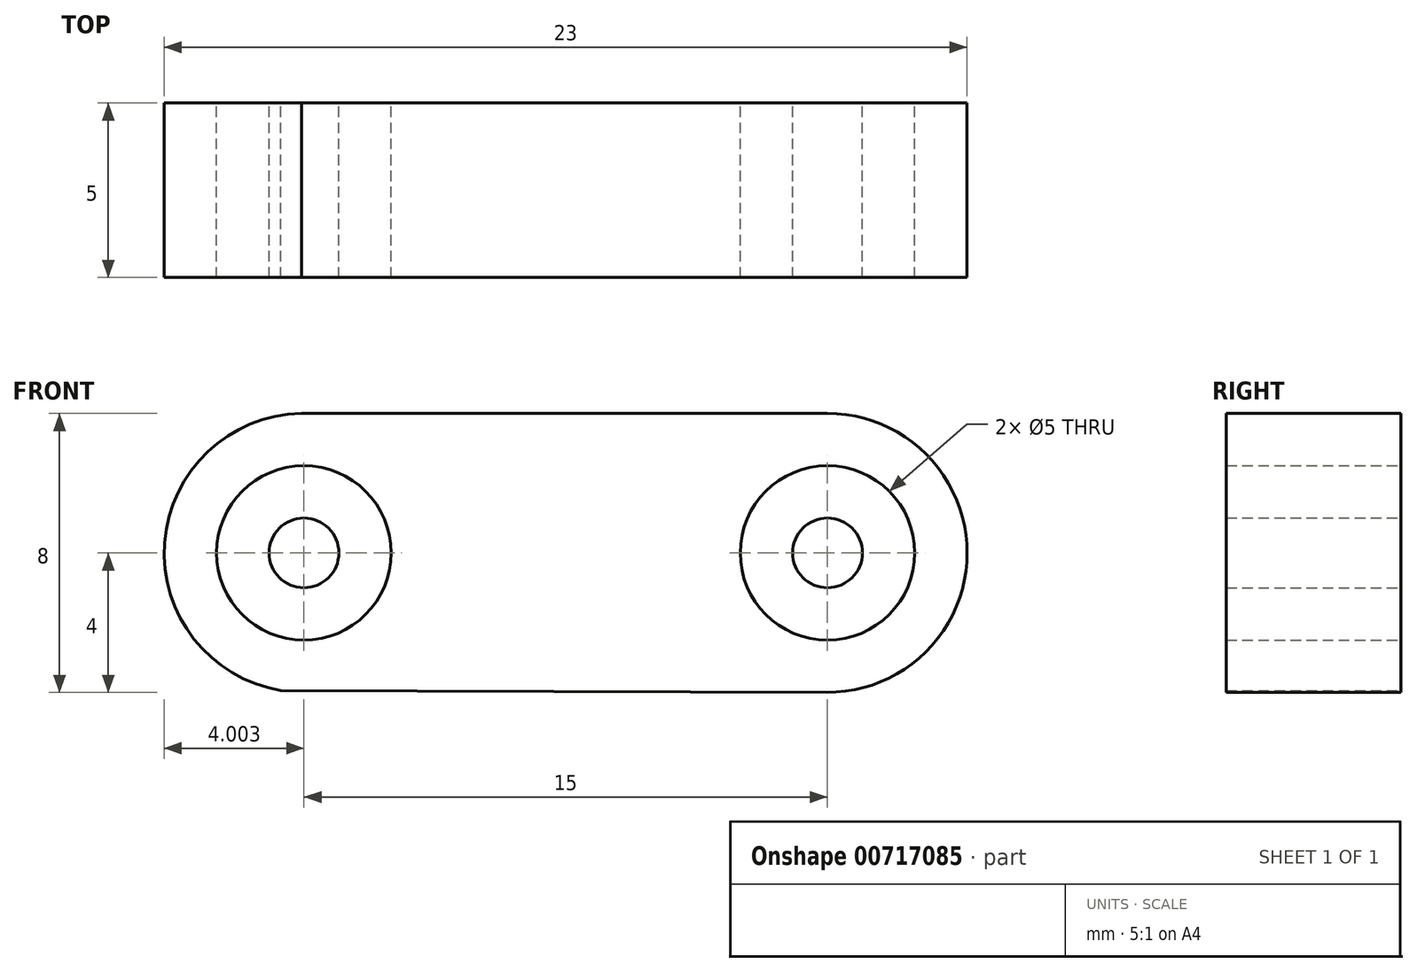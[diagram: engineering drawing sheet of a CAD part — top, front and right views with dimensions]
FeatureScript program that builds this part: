
annotation { "Feature Type Name" : "Feature", "Feature Type Description" : "" }
export const myFeature = defineFeature(function(context is Context, id is Id, definition is map)
    precondition{}
    {
        {
            var Q0;
            Q0=qCreatedBy(makeId("Front.planeOp"),FACE);
            var sketch = newSketch(context, id + "F0", { "sketchPlane" : qUnion([Q0])});
            skLineSegment(sketch, "E0", {"start": v(-11.39, 16.4) * mm, "end": v(3.61, 16.4) * mm});
            skCircle(sketch, "E1", {"center": v(-11.39, 16.4) * mm, "radius": 2.5 * mm});
            skArc(sketch, "E2", {"start": v(-11.31, 20.4) * mm, "mid": v(-15.38, 16.12) * mm, "end": v(-10.75, 12.45) * mm});
            skCircle(sketch, "E3", {"center": v(3.61, 16.4) * mm, "radius": 2.5 * mm});
            skArc(sketch, "E4", {"start": v(3.6, 12.4) * mm, "mid": v(7.61, 16.4) * mm, "end": v(3.61, 20.4) * mm});
            skLineSegment(sketch, "E5", {"start": v(-11.46, 20.4) * mm, "end": v(3.61, 20.4) * mm});
            skLineSegment(sketch, "E6", {"start": v(-12.05, 12.46) * mm, "end": v(3.6, 12.4) * mm});
            skCircle(sketch, "E7", {"center": v(-11.39, 16.4) * mm, "radius": 1 * mm});
            skCircle(sketch, "E8", {"center": v(3.61, 16.4) * mm, "radius": 1 * mm});
            skSolve(sketch);
        }
        {
            var Q0;
            Q0=makeQuery(id+"F0.imprint","IMPRINT",FACE,{"disambiguationData":[TD([[makeQuery(id+"F0.imprint","IMPRINT",EDGE,{"derivedFrom":sQuery(id+"F0.wireOp",EDGE,"E1")}),-1.0]])]});
            extrude(context, id + "F1", {"entities" : qUnion([Q0]), "depth" : 5 * mm, "offsetDistance" : 25.4 * mm});
        }
        {
            var Q0;
            Q0=makeQuery(id+"F0.imprint","IMPRINT",FACE,{"disambiguationData":[TD([[makeQuery(id+"F0.imprint","IMPRINT",EDGE,{"derivedFrom":sQuery(id+"F0.wireOp",EDGE,"E7")}),1.0]])]});
            var Q1;
            Q1=makeQuery(id+"F0.imprint","IMPRINT",FACE,{"disambiguationData":[TD([[makeQuery(id+"F0.imprint","IMPRINT",EDGE,{"derivedFrom":sQuery(id+"F0.wireOp",EDGE,"E8")}),1.0]])]});
            extrude(context, id + "F2", {"entities" : qUnion([Q0, Q1]), "depth" : 5 * mm, "offsetDistance" : 25.4 * mm});
        }
    });
